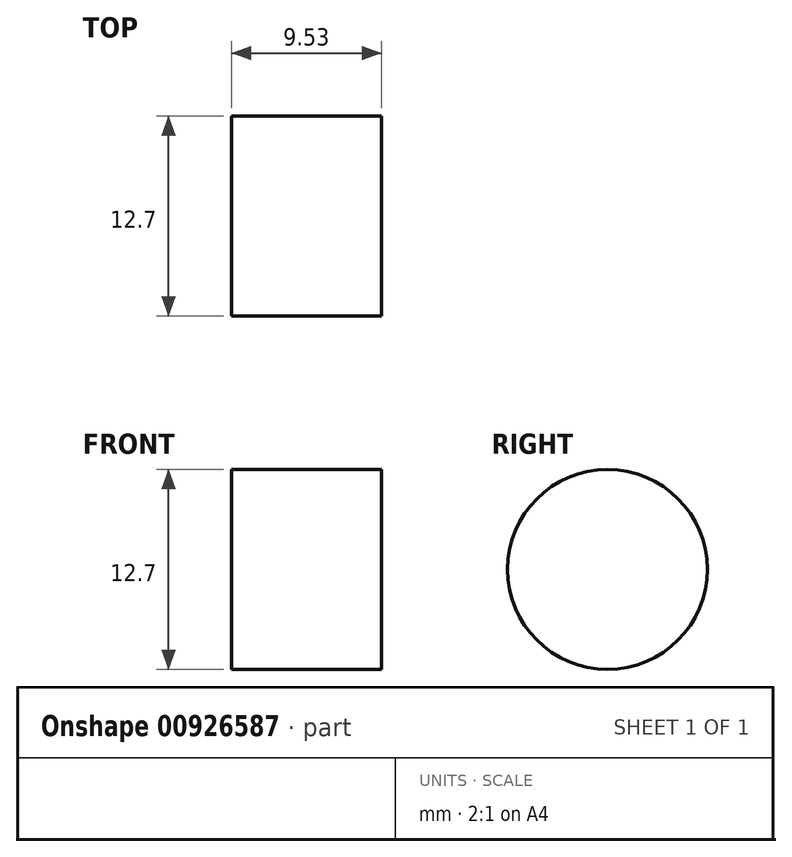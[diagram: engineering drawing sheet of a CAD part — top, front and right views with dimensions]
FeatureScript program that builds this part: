
annotation { "Feature Type Name" : "Feature", "Feature Type Description" : "" }
export const myFeature = defineFeature(function(context is Context, id is Id, definition is map)
    precondition{}
    {
        {
            var Q0;
            Q0=qCreatedBy(makeId("Front.planeOp"),FACE);
            var sketch = newSketch(context, id + "F0", { "sketchPlane" : qUnion([Q0])});
            skLineSegment(sketch, "E0", {"start": v(-106.6, 0) * mm, "end": v(-106.6, 457.2) * mm});
            skLineSegment(sketch, "E1", {"start": v(-106.6, 0) * mm, "end": v(-116.12, 0) * mm});
            skLineSegment(sketch, "E2", {"start": v(-116.12, 0) * mm, "end": v(-116.12, 457.2) * mm});
            skLineSegment(sketch, "E3", {"start": v(-106.6, 0) * mm, "end": v(0, 0) * mm, "construction": true});
            skLineSegment(sketch, "E4", {"start": v(-116.12, 457.2) * mm, "end": v(-106.6, 457.2) * mm});
            skSolve(sketch);
        }
        {
            var Q0;
            Q0=makeQuery(id+"F0.imprint","IMPRINT",FACE,{"disambiguationData":[TD([[makeQuery(id+"F0.imprint","IMPRINT",EDGE,{"derivedFrom":sQuery(id+"F0.wireOp",EDGE,"E0")}),1.0]])]});
            extrude(context, id + "F1", {"entities" : qUnion([Q0]), "depth" : 304.8 * mm, "offsetDistance" : 25.4 * mm});
        }
        {
            var Q0;
            Q0=qCreatedBy(makeId("Front.planeOp"),FACE);
            var sketch = newSketch(context, id + "F2", { "sketchPlane" : qUnion([Q0])});
            skLineSegment(sketch, "E5.bottom", {"start": v(241.52, 240.9) * mm, "end": v(-63.28, 240.9) * mm});
            skLineSegment(sketch, "E5.top", {"start": v(241.52, -63.9) * mm, "end": v(-63.28, -63.9) * mm});
            skLineSegment(sketch, "E5.left", {"start": v(241.52, 240.9) * mm, "end": v(241.52, -63.9) * mm});
            skLineSegment(sketch, "E5.right", {"start": v(-63.28, 240.9) * mm, "end": v(-63.28, -63.9) * mm});
            skSolve(sketch);
        }
        {
            var Q0;
            Q0=makeQuery(id+"F1.opExtrude","SWEPT_FACE",FACE,{"disambiguationData":[OSD([sQuery(id+"F0.wireOp",EDGE,"E2")])]});
            var sketch = newSketch(context, id + "F3", { "sketchPlane" : qUnion([Q0])});
            skCircle(sketch, "E6", {"center": v(38.1, 37.7) * mm, "radius": 6.35 * mm});
            skCircle(sketch, "E7", {"center": v(266.71, 37.7) * mm, "radius": 6.35 * mm});
            skLineSegment(sketch, "E8", {"start": v(0, 37.7) * mm, "end": v(38.1, 37.7) * mm, "construction": true});
            skLineSegment(sketch, "E9", {"start": v(266.71, 37.7) * mm, "end": v(304.8, 38.76) * mm, "construction": true});
            skLineSegment(sketch, "E10", {"start": v(266.71, 37.7) * mm, "end": v(266.71, 0) * mm, "construction": true});
            skLineSegment(sketch, "E11", {"start": v(38.1, 37.7) * mm, "end": v(38.1, 0) * mm, "construction": true});
            skSolve(sketch);
        }
        {
            var Q0;
            Q0=makeQuery(id+"F3.imprint","IMPRINT",FACE,{"disambiguationData":[TD([[makeQuery(id+"F3.imprint","IMPRINT",EDGE,{"derivedFrom":sQuery(id+"F3.wireOp",EDGE,"E6")}),-1.0]])]});
            var Q1;
            Q1=makeQuery(id+"F3.imprint","IMPRINT",FACE,{"disambiguationData":[TD([[makeQuery(id+"F3.imprint","IMPRINT",EDGE,{"derivedFrom":sQuery(id+"F3.wireOp",EDGE,"E7")}),1.0]])]});
            extrude(context, id + "F4", {"entities" : qUnion([Q0, Q1]), "operationType" : NewBodyOperationType.REMOVE, "endBound" : BoundingType.THROUGH_ALL, "oppositeDirection" : true, "depth" : 25.4 * mm, "offsetDistance" : 25.4 * mm});
        }
        {
            var Q0;
            Q0=makeQuery(id+"F1.opExtrude","SWEPT_FACE",FACE,{"disambiguationData":[OSD([sQuery(id+"F0.wireOp",EDGE,"E2")])]});
            var sketch = newSketch(context, id + "F5", { "sketchPlane" : qUnion([Q0])});
            skCircle(sketch, "E12", {"center": v(100.01, 247.65) * mm, "radius": 4.78 * mm});
            skCircle(sketch, "E13", {"center": v(204.79, 247.65) * mm, "radius": 4.78 * mm});
            skCircle(sketch, "E14", {"center": v(100.01, 228.6) * mm, "radius": 4.78 * mm});
            skCircle(sketch, "E15", {"center": v(204.79, 228.6) * mm, "radius": 4.78 * mm});
            skLineSegment(sketch, "E16", {"start": v(0, 247.65) * mm, "end": v(100.01, 247.65) * mm, "construction": true});
            skLineSegment(sketch, "E17", {"start": v(0, 228.6) * mm, "end": v(100.01, 228.6) * mm, "construction": true});
            skLineSegment(sketch, "E18", {"start": v(204.79, 247.65) * mm, "end": v(304.8, 247.65) * mm, "construction": true});
            skLineSegment(sketch, "E19", {"start": v(204.79, 228.6) * mm, "end": v(304.8, 228.6) * mm, "construction": true});
            skLineSegment(sketch, "E20", {"start": v(100.01, 247.65) * mm, "end": v(204.79, 247.65) * mm, "construction": true});
            skLineSegment(sketch, "E21", {"start": v(100.01, 228.6) * mm, "end": v(204.79, 228.6) * mm, "construction": true});
            skLineSegment(sketch, "E22", {"start": v(100.01, 247.65) * mm, "end": v(100.01, 228.6) * mm, "construction": true});
            skCircle(sketch, "E23", {"center": v(100.01, 209.55) * mm, "radius": 4.78 * mm});
            skCircle(sketch, "E24", {"center": v(204.79, 209.55) * mm, "radius": 4.78 * mm});
            skLineSegment(sketch, "E25", {"start": v(100.01, 228.6) * mm, "end": v(100.01, 209.55) * mm, "construction": true});
            skLineSegment(sketch, "E26", {"start": v(100.01, 209.55) * mm, "end": v(204.79, 209.55) * mm, "construction": true});
            skSolve(sketch);
        }
        {
            var Q0;
            Q0=makeQuery(id+"F5.imprint","IMPRINT",FACE,{"disambiguationData":[TD([[makeQuery(id+"F5.imprint","IMPRINT",EDGE,{"derivedFrom":sQuery(id+"F5.wireOp",EDGE,"E12")}),1.0]])]});
            var Q1;
            Q1=makeQuery(id+"F5.imprint","IMPRINT",FACE,{"disambiguationData":[TD([[makeQuery(id+"F5.imprint","IMPRINT",EDGE,{"derivedFrom":sQuery(id+"F5.wireOp",EDGE,"E13")}),1.0]])]});
            var Q2;
            Q2=makeQuery(id+"F5.imprint","IMPRINT",FACE,{"disambiguationData":[TD([[makeQuery(id+"F5.imprint","IMPRINT",EDGE,{"derivedFrom":sQuery(id+"F5.wireOp",EDGE,"E14")}),1.0]])]});
            var Q3;
            Q3=makeQuery(id+"F5.imprint","IMPRINT",FACE,{"disambiguationData":[TD([[makeQuery(id+"F5.imprint","IMPRINT",EDGE,{"derivedFrom":sQuery(id+"F5.wireOp",EDGE,"E15")}),1.0]])]});
            var Q4;
            Q4=makeQuery(id+"F5.imprint","IMPRINT",FACE,{"disambiguationData":[TD([[makeQuery(id+"F5.imprint","IMPRINT",EDGE,{"derivedFrom":sQuery(id+"F5.wireOp",EDGE,"E23")}),1.0]])]});
            var Q5;
            Q5=makeQuery(id+"F5.imprint","IMPRINT",FACE,{"disambiguationData":[TD([[makeQuery(id+"F5.imprint","IMPRINT",EDGE,{"derivedFrom":sQuery(id+"F5.wireOp",EDGE,"E24")}),1.0]])]});
            extrude(context, id + "F6", {"entities" : qUnion([Q0, Q1, Q2, Q3, Q4, Q5]), "operationType" : NewBodyOperationType.REMOVE, "endBound" : BoundingType.THROUGH_ALL, "oppositeDirection" : true, "depth" : 25.4 * mm, "offsetDistance" : 25.4 * mm});
        }
    });
